# Revit family: Basin-Caroma Track Inset Vanity
name_source: partatom
category: Plumbing Fixtures
revit_build: Autodesk Revit Architecture 2012 (Build: 20110309_2315(x64)
units: mm (PartAtom-declared; Revit-internal decimal feet)

## types (1)
- Track Inset - 3 Tap Holes
    1 Taphole = No
    3 Tapholes = Yes
    CW Connection = No
    Default Elevation = 1219 mm
    Description = Track Inset Vanity Basin
    HW Connection = No
    Manufacturer = Caroma
    Model = 633535
    PlumbingMaterial_ANZRS = Porcelain-White-Caroma
    Spout Penetration = 0 mm  [stored 0 ft]
    Tap Penetrations = 0 mm  [stored 0 ft]
    Type Comments = Vitreous China Inset Vanity Basin
    URL = www.caroma.com.au
    Vent Connection = No
    Waste = Metal-Chrome-Caroma
    Waste Connection = Yes

note: [stored X ft] marks values corroborated as IEEE doubles in the binary element streams (Revit-internal decimal feet)

## geometry (parser evidence)
native form markers: Blend x8, Sweep x1
no freeform markers — native parametric forms only
